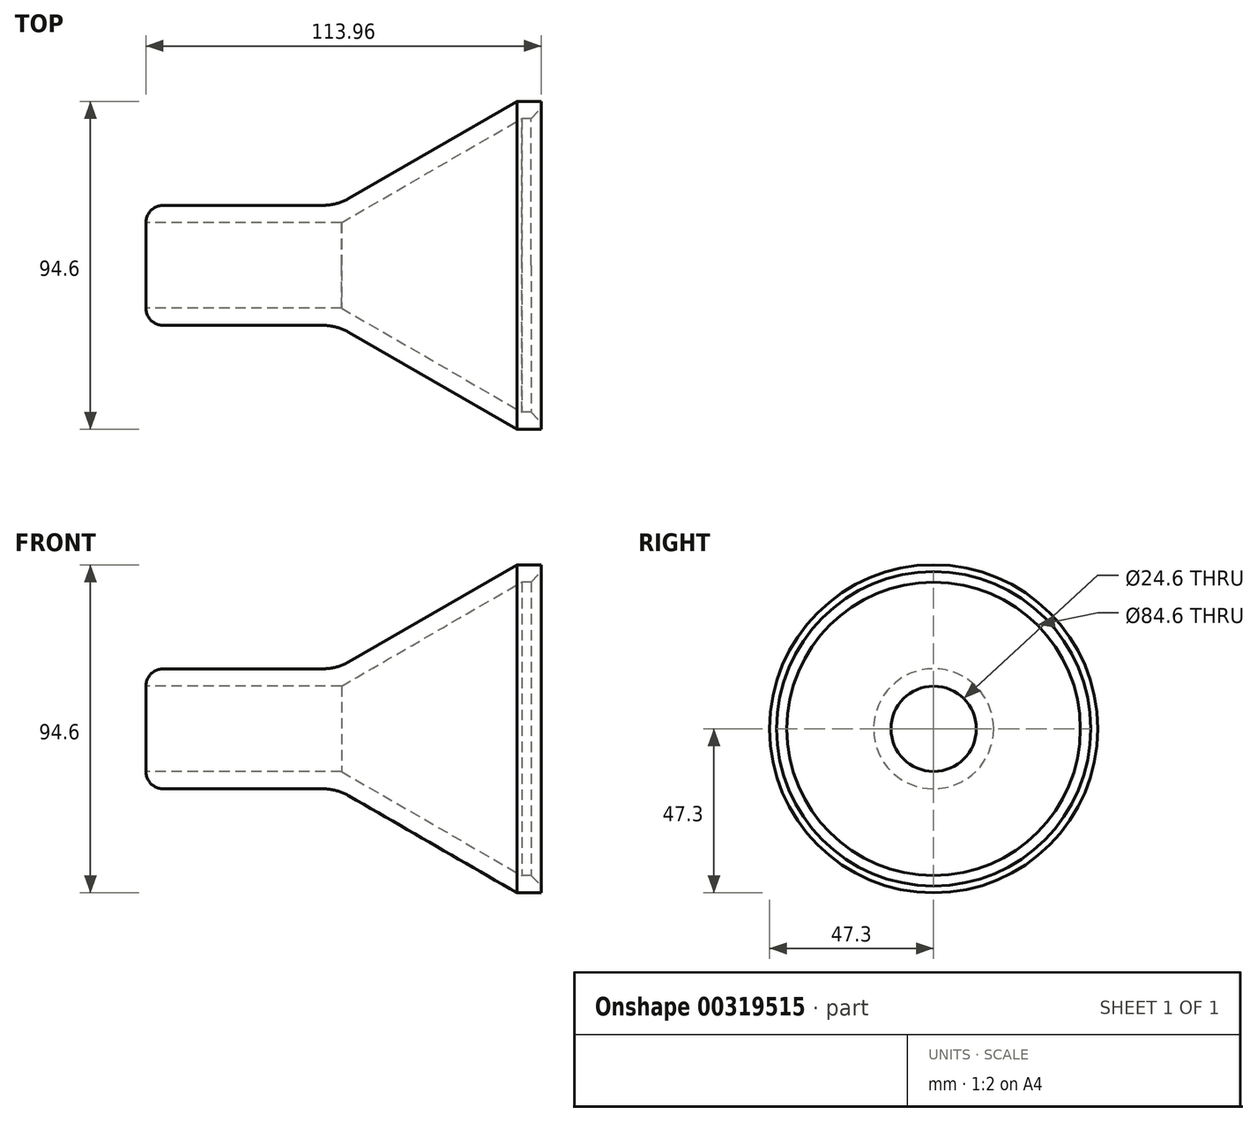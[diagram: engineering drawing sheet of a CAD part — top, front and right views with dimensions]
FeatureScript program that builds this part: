
annotation { "Feature Type Name" : "Feature", "Feature Type Description" : "" }
export const myFeature = defineFeature(function(context is Context, id is Id, definition is map)
    precondition{}
    {
        {
            var Q0;
            Q0=qCreatedBy(makeId("Front.planeOp"),FACE);
            var sketch = newSketch(context, id + "F0", { "sketchPlane" : qUnion([Q0])});
            skLineSegment(sketch, "E0", {"start": v(0, 0) * mm, "end": v(38.4, 0) * mm, "construction": true});
            skLineSegment(sketch, "E1", {"start": v(0, 17.3) * mm, "end": v(55, 17.3) * mm});
            skLineSegment(sketch, "E2", {"start": v(55, 17.3) * mm, "end": v(106.96, 47.3) * mm});
            skLineSegment(sketch, "E3", {"start": v(0, 12.3) * mm, "end": v(0, 17.3) * mm});
            skLineSegment(sketch, "E4", {"start": v(106.96, 47.3) * mm, "end": v(113.96, 47.3) * mm});
            skLineSegment(sketch, "E5.0", {"start": v(108.3, 42.3) * mm, "end": v(113.96, 42.3) * mm});
            skLineSegment(sketch, "E5.1", {"start": v(56.34, 12.3) * mm, "end": v(108.3, 42.3) * mm});
            skLineSegment(sketch, "E5.2", {"start": v(0, 12.3) * mm, "end": v(56.34, 12.3) * mm});
            skLineSegment(sketch, "E6", {"start": v(113.96, 47.3) * mm, "end": v(113.96, 42.3) * mm});
            skSolve(sketch);
        }
        {
            var Q0;
            Q0=makeQuery(id+"F0.imprint","IMPRINT",FACE,{"disambiguationData":[TD([[makeQuery(id+"F0.imprint","IMPRINT",EDGE,{"derivedFrom":sQuery(id+"F0.wireOp",EDGE,"E1")}),-1.0]])]});
            var Q1;
            Q1=sQuery(id+"F0.wireOp",EDGE,"E0");
            revolve(context, id + "F1", {"entities" : qUnion([Q0]), "axis" : qUnion([Q1]), "revolveType" : RevolveType.FULL});
        }
        {
            var Q0;
            Q0=makeQuery(id+"F1.opRevolve","SWEPT_EDGE",EDGE,{"disambiguationData":[OSD([sQuery(id+"F0.wireOp",EDGE,"E5.0"),sQuery(id+"F0.wireOp",EDGE,"E6")])]});
            chamfer(context, id + "F2", {"entities" : qUnion([Q0]), "width" : 3 * mm, "tangentPropagation" : true});
        }
        {
            var Q0;
            Q0=makeQuery(id+"F1.opRevolve","SWEPT_EDGE",EDGE,{"disambiguationData":[OSD([sQuery(id+"F0.wireOp",EDGE,"E1"),sQuery(id+"F0.wireOp",EDGE,"E2")])]});
            fillet(context, id + "F3", {"entities" : qUnion([Q0]), "radius" : 15 * mm, "tangentPropagation" : true, "allowEdgeOverflow" : false});
        }
        {
            var Q0;
            Q0=makeQuery(id+"F1.opRevolve","SWEPT_EDGE",EDGE,{"disambiguationData":[OSD([sQuery(id+"F0.wireOp",EDGE,"E1"),sQuery(id+"F0.wireOp",EDGE,"E3")])]});
            fillet(context, id + "F4", {"entities" : qUnion([Q0]), "radius" : 5 * mm, "tangentPropagation" : true, "allowEdgeOverflow" : false});
        }
    });
